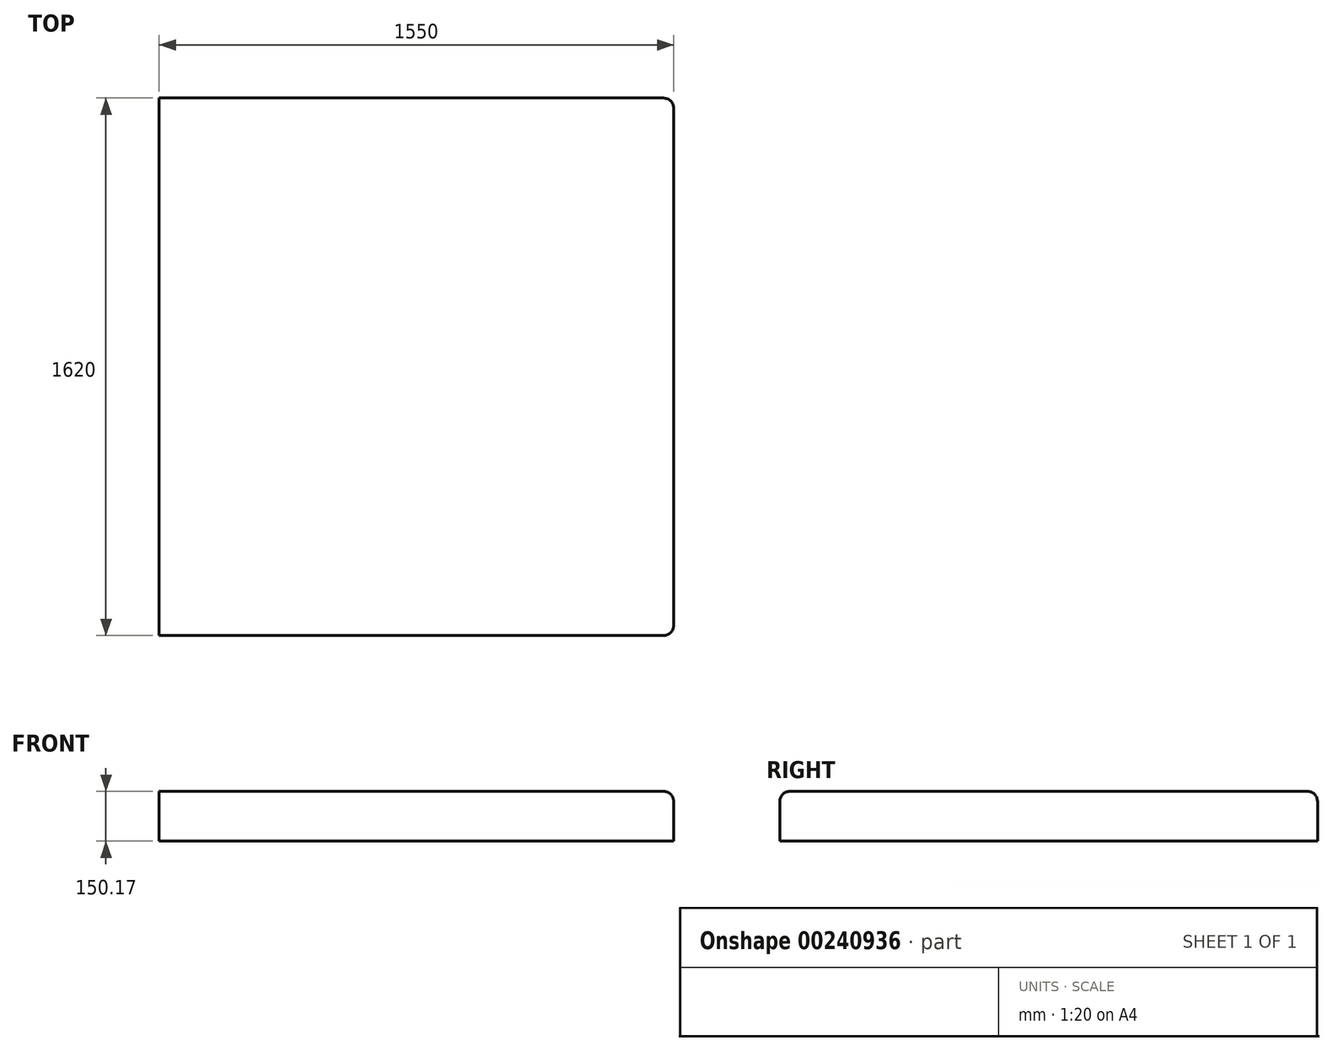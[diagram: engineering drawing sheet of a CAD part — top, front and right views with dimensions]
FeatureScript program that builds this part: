
annotation { "Feature Type Name" : "Feature", "Feature Type Description" : "" }
export const myFeature = defineFeature(function(context is Context, id is Id, definition is map)
    precondition{}
    {
        {
            var Q0;
            Q0=qCreatedBy(makeId("Right.planeOp"),FACE);
            var sketch = newSketch(context, id + "F0", { "sketchPlane" : qUnion([Q0])});
            skLineSegment(sketch, "E0.bottom", {"start": v(825.93, 61.13) * mm, "end": v(-794.07, 61.13) * mm});
            skLineSegment(sketch, "E0.top", {"start": v(825.93, 211.3) * mm, "end": v(-794.07, 211.3) * mm});
            skLineSegment(sketch, "E0.left", {"start": v(825.93, 61.13) * mm, "end": v(825.93, 211.3) * mm});
            skLineSegment(sketch, "E0.right", {"start": v(-794.07, 61.13) * mm, "end": v(-794.07, 211.3) * mm});
            skSolve(sketch);
        }
        {
            var Q0;
            Q0 = qSketchRegion(id + "F0", true);
            extrude(context, id + "F1", {"entities" : qUnion([Q0]), "oppositeDirection" : true, "depth" : 500 * mm});
        }
        {
            var Q0;
            Q0 = qSketchRegion(id + "F0", true);
            extrude(context, id + "F2", {"entities" : qUnion([Q0]), "operationType" : NewBodyOperationType.ADD, "depth" : 1050 * mm});
        }
        {
            var Q0;
            {var subQ0=sQuery(id+"F0.wireOp",EDGE,"E0.right");var subQ1=sQuery(id+"F0.wireOp",EDGE,"E0.top");Q0=makeQuery(id+"F2.boolean.opBoolean","MERGE",EDGE,{"derivedFrom":[makeQuery(id+"F1.opExtrude","SWEPT_EDGE",EDGE,{"disambiguationData":[OSD([subQ1,subQ0])]}),makeQuery(id+"F2.opExtrude","SWEPT_EDGE",EDGE,{"disambiguationData":[OSD([subQ1,subQ0])]})]});}
            var Q1;
            Q1=makeQuery(id+"F2.opExtrude","CAP_EDGE",EDGE,{"disambiguationData":[OSD([sQuery(id+"F0.wireOp",EDGE,"E0.right")])],"isStart":false});
            var Q2;
            Q2=makeQuery(id+"F2.opExtrude","CAP_EDGE",EDGE,{"disambiguationData":[OSD([sQuery(id+"F0.wireOp",EDGE,"E0.top")])],"isStart":false});
            var Q3;
            Q3=makeQuery(id+"F2.opExtrude","CAP_EDGE",EDGE,{"disambiguationData":[OSD([sQuery(id+"F0.wireOp",EDGE,"E0.left")])],"isStart":false});
            var Q4;
            {var subQ0=sQuery(id+"F0.wireOp",EDGE,"E0.left");var subQ1=sQuery(id+"F0.wireOp",EDGE,"E0.top");Q4=makeQuery(id+"F2.boolean.opBoolean","MERGE",EDGE,{"derivedFrom":[makeQuery(id+"F1.opExtrude","SWEPT_EDGE",EDGE,{"disambiguationData":[OSD([subQ1,subQ0])]}),makeQuery(id+"F2.opExtrude","SWEPT_EDGE",EDGE,{"disambiguationData":[OSD([subQ1,subQ0])]})]});}
            fillet(context, id + "F3", {"entities" : qUnion([Q0, Q1, Q2, Q3, Q4]), "radius" : 30 * mm, "tangentPropagation" : true, "allowEdgeOverflow" : false});
        }
    });
